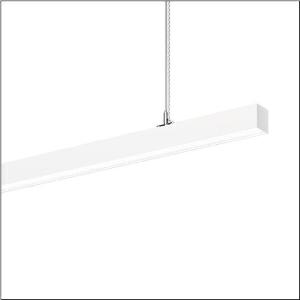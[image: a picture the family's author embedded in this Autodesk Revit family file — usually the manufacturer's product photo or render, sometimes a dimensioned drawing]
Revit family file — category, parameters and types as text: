
# Revit family: silica_r__21_51mx30dc39wb_5262
name_source: partatom
category: Lighting Fixtures
units: mm (PartAtom-declared; Revit-internal decimal feet)

## family parameters
Cut with Voids When Loaded = No
Host = Face
Light Source = No
Part Type = Normal
Room Calculation Point = No
Round Connector Dimension = Use Diameter
Shared = No

## types (1)
- --- (1 x LED, 10520 lm, 68.3 W, 3000K)
    Apparent Load = 68 VA
    CIE Flux Codes = 47 79 96 57 100
    Color Rendering = 80
    Color Temperature = 3000K
    Default Elevation = 1800 mm
    Description = Silica® 21, office luminaire, primary optical cover: cover, of PMMA, opal, light emission: direct/indirect distribution, primary light characteristic: symmetric, installation type: suspended mounting, LED, rated luminous flux: 10.520lm, luminous efficacy: 154lm/W, light colour: 830, colour temperature: 3000K, with terminal, 3+2-pole, max. 2.5mm², mains connection: 220..240V, AC, 50/60Hz, rated input power: 68.3W, luminaire housing, of aluminium, traffic white (RAL 9016), length: 3.004mm, width: 53mm, height: 53mm, protection rating (complete): IP20, insulation class (complete): insulation class I (protective earthing), certification: CE, permissible operating ambient temperature: 0..+35°C, standard: EN 50419, packaging unit: 1 piece
    Height = 53 mm
    Lamp = 1 x LED
    Lamp Light Flux = 10520 lm
    Lamp Power = 68.3 W
    Lamp count = 1
    Length = 3004 mm
    Luminous efficacy = 154 lm/W
    Manufacturer = Siteco
    ModVariant = No
    Model = 51MX30DC39WB
    Mounting Place = Ceiling
    Mounting Type = Pendant
    Number of Poles = 1
    OnlyDefault = Yes
    Power Factor = 1
    Product Name = Silica® 21
    Product group = office luminaire | ceiling pendant
    ProductGroupID = 902
    Protection Class = Protection class I
    Protection Degree = IP 20
    RLX_Detail_Level = 1
    RLX_Emergency_Light_Flux = 0 lm
    RLX_Emergency_Type = 0
    RLX_Emergency_Type_DB = No
    RlxData = <blob elided: 21361 chars, md5=633358ec>
    Socket = socket
    Standby Power = 0 W
    System Light Flux = 10520 lm
    System Power = 68 W
    Type Comments = factory setting: luminous flux: 100 % | dim-lin: 254 | 233 mA
    Type Image = l_1335916.jpg
    URL = http://relux.com
    VarID = @adj_086237
    Voltage = 0 V
    Weight = 0.00 kg
    Width = 53 mm

## geometry (parser evidence)
native form markers: Blend x4, Sweep x14
no freeform markers — native parametric forms only
